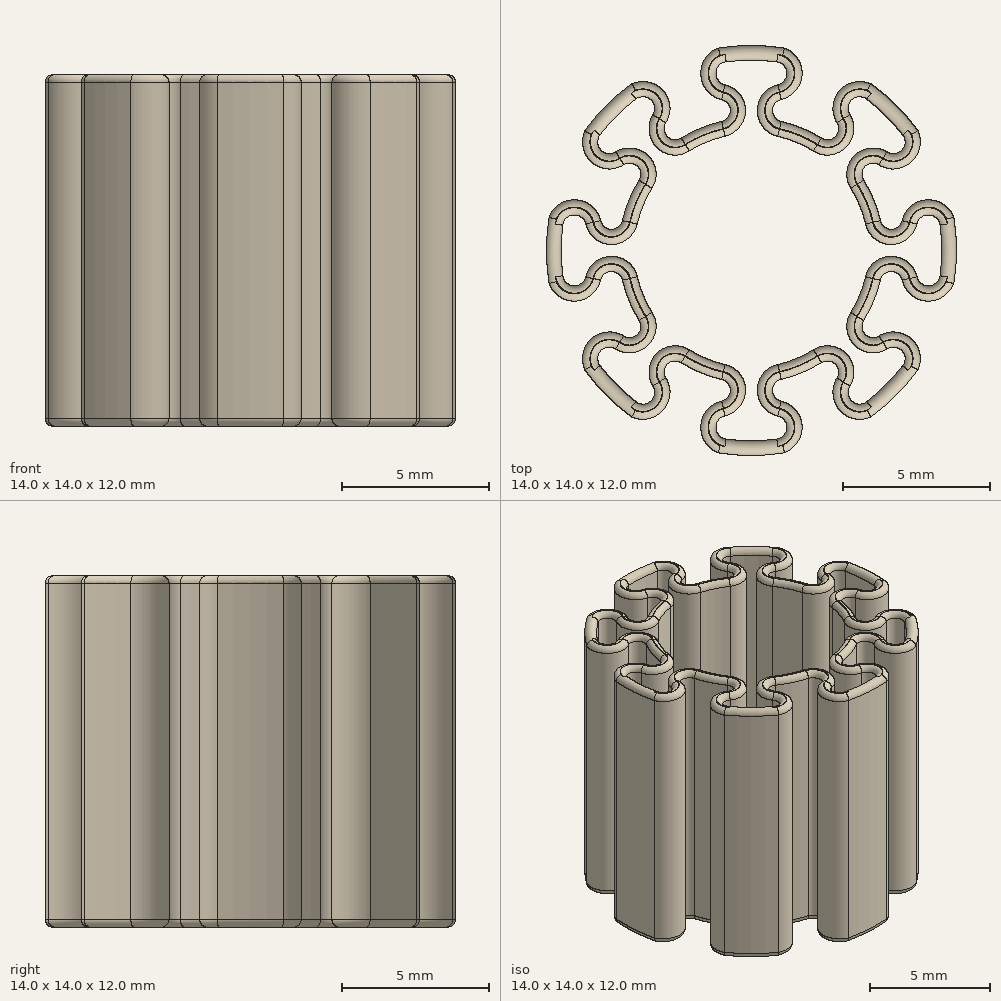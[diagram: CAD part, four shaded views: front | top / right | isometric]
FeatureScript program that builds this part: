
annotation { "Feature Type Name" : "Feature", "Feature Type Description" : "" }
export const myFeature = defineFeature(function(context is Context, id is Id, definition is map)
    precondition{}
    {
        {
            var Q0;
            Q0=qCreatedBy(makeId("Top.planeOp"),FACE);
            var sketch = newSketch(context, id + "F0", { "sketchPlane" : qUnion([Q0])});
            skArc(sketch, "E0", {"start": v(-4.08, 5.68) * mm, "mid": v(-4.95, 4.95) * mm, "end": v(-5.68, 4.08) * mm});
            skArc(sketch, "E1", {"start": v(-0.9, 3.9) * mm, "mid": v(-1.53, 3.7) * mm, "end": v(-2.12, 3.4) * mm});
            skArc(sketch, "E2", {"start": v(-4.1, 5.36) * mm, "mid": v(-4.77, 4.77) * mm, "end": v(-5.36, 4.1) * mm, "construction": true});
            skArc(sketch, "E3", {"start": v(-0.96, 4.14) * mm, "mid": v(-1.63, 3.93) * mm, "end": v(-2.25, 3.6) * mm, "construction": true});
            skArc(sketch, "E4", {"start": v(0.96, 5.41) * mm, "mid": v(1.46, 6.08) * mm, "end": v(0.9, 6.7) * mm, "construction": true});
            skArc(sketch, "E5", {"start": v(0.96, 5.41) * mm, "mid": v(0.45, 4.78) * mm, "end": v(0.96, 4.14) * mm, "construction": true});
            skArc(sketch, "E6", {"start": v(-0.9, 6.7) * mm, "mid": v(-1.46, 6.08) * mm, "end": v(-0.96, 5.41) * mm, "construction": true});
            skArc(sketch, "E7", {"start": v(-0.96, 4.14) * mm, "mid": v(-0.45, 4.78) * mm, "end": v(-0.96, 5.41) * mm, "construction": true});
            skLineSegment(sketch, "E8", {"start": v(0, 0) * mm, "end": v(0, 7.77) * mm, "construction": true});
            skArc(sketch, "E9.1.0", {"start": v(-3.15, 4.5) * mm, "mid": v(-3.06, 3.7) * mm, "end": v(-2.25, 3.6) * mm, "construction": true});
            skArc(sketch, "E9.1.1", {"start": v(-3.15, 4.5) * mm, "mid": v(-3.26, 5.33) * mm, "end": v(-4.1, 5.36) * mm, "construction": true});
            skArc(sketch, "E9.1.2", {"start": v(-3.6, 2.25) * mm, "mid": v(-3.7, 3.06) * mm, "end": v(-4.5, 3.15) * mm, "construction": true});
            skArc(sketch, "E9.1.3", {"start": v(-5.36, 4.1) * mm, "mid": v(-5.33, 3.26) * mm, "end": v(-4.5, 3.15) * mm, "construction": true});
            skArc(sketch, "E9.2.0", {"start": v(-5.41, 0.96) * mm, "mid": v(-4.78, 0.45) * mm, "end": v(-4.14, 0.96) * mm, "construction": true});
            skArc(sketch, "E9.2.1", {"start": v(-5.41, 0.96) * mm, "mid": v(-6.08, 1.46) * mm, "end": v(-6.7, 0.9) * mm, "construction": true});
            skArc(sketch, "E9.2.2", {"start": v(-4.14, -0.96) * mm, "mid": v(-4.78, -0.45) * mm, "end": v(-5.41, -0.96) * mm, "construction": true});
            skArc(sketch, "E9.2.3", {"start": v(-6.7, -0.9) * mm, "mid": v(-6.08, -1.46) * mm, "end": v(-5.41, -0.96) * mm, "construction": true});
            skArc(sketch, "E9.3.0", {"start": v(-4.5, -3.15) * mm, "mid": v(-3.7, -3.06) * mm, "end": v(-3.6, -2.25) * mm, "construction": true});
            skArc(sketch, "E9.3.1", {"start": v(-4.5, -3.15) * mm, "mid": v(-5.33, -3.26) * mm, "end": v(-5.36, -4.1) * mm, "construction": true});
            skArc(sketch, "E9.3.2", {"start": v(-2.25, -3.6) * mm, "mid": v(-3.06, -3.7) * mm, "end": v(-3.15, -4.5) * mm, "construction": true});
            skArc(sketch, "E9.3.3", {"start": v(-4.1, -5.36) * mm, "mid": v(-3.26, -5.33) * mm, "end": v(-3.15, -4.5) * mm, "construction": true});
            skArc(sketch, "E9.4.0", {"start": v(-0.96, -5.41) * mm, "mid": v(-0.45, -4.78) * mm, "end": v(-0.96, -4.14) * mm, "construction": true});
            skArc(sketch, "E9.4.1", {"start": v(-0.96, -5.41) * mm, "mid": v(-1.46, -6.08) * mm, "end": v(-0.9, -6.7) * mm, "construction": true});
            skArc(sketch, "E9.4.2", {"start": v(0.96, -4.14) * mm, "mid": v(0.45, -4.78) * mm, "end": v(0.96, -5.41) * mm, "construction": true});
            skArc(sketch, "E9.4.3", {"start": v(0.9, -6.7) * mm, "mid": v(1.46, -6.08) * mm, "end": v(0.96, -5.41) * mm, "construction": true});
            skArc(sketch, "E9.5.0", {"start": v(3.15, -4.5) * mm, "mid": v(3.06, -3.7) * mm, "end": v(2.25, -3.6) * mm, "construction": true});
            skArc(sketch, "E9.5.1", {"start": v(3.15, -4.5) * mm, "mid": v(3.26, -5.33) * mm, "end": v(4.1, -5.36) * mm, "construction": true});
            skArc(sketch, "E9.5.2", {"start": v(3.6, -2.25) * mm, "mid": v(3.7, -3.06) * mm, "end": v(4.5, -3.15) * mm, "construction": true});
            skArc(sketch, "E9.5.3", {"start": v(5.36, -4.1) * mm, "mid": v(5.33, -3.26) * mm, "end": v(4.5, -3.15) * mm, "construction": true});
            skArc(sketch, "E9.6.0", {"start": v(5.41, -0.96) * mm, "mid": v(4.78, -0.45) * mm, "end": v(4.14, -0.96) * mm, "construction": true});
            skArc(sketch, "E9.6.1", {"start": v(5.41, -0.96) * mm, "mid": v(6.08, -1.46) * mm, "end": v(6.7, -0.9) * mm, "construction": true});
            skArc(sketch, "E9.6.2", {"start": v(4.14, 0.96) * mm, "mid": v(4.78, 0.45) * mm, "end": v(5.41, 0.96) * mm, "construction": true});
            skArc(sketch, "E9.6.3", {"start": v(6.7, 0.9) * mm, "mid": v(6.08, 1.46) * mm, "end": v(5.41, 0.96) * mm, "construction": true});
            skArc(sketch, "E9.7.0", {"start": v(4.5, 3.15) * mm, "mid": v(3.7, 3.06) * mm, "end": v(3.6, 2.25) * mm, "construction": true});
            skArc(sketch, "E9.7.1", {"start": v(4.5, 3.15) * mm, "mid": v(5.33, 3.26) * mm, "end": v(5.36, 4.1) * mm, "construction": true});
            skArc(sketch, "E9.7.2", {"start": v(2.25, 3.6) * mm, "mid": v(3.06, 3.7) * mm, "end": v(3.15, 4.5) * mm, "construction": true});
            skArc(sketch, "E9.7.3", {"start": v(4.1, 5.36) * mm, "mid": v(3.26, 5.33) * mm, "end": v(3.15, 4.5) * mm, "construction": true});
            skLineSegment(sketch, "E10", {"start": v(-0.8, 6.04) * mm, "end": v(0.8, 6.04) * mm, "construction": true});
            skLineSegment(sketch, "E11", {"start": v(1.1, 4.78) * mm, "end": v(2.6, 4.16) * mm, "construction": true});
            skArc(sketch, "E12.trimOffspring", {"start": v(2.25, 3.6) * mm, "mid": v(1.63, 3.93) * mm, "end": v(0.96, 4.14) * mm, "construction": true});
            skArc(sketch, "E13.trimOffspring", {"start": v(4.14, 0.96) * mm, "mid": v(3.93, 1.63) * mm, "end": v(3.6, 2.25) * mm, "construction": true});
            skArc(sketch, "E14.trimOffspring", {"start": v(3.6, -2.25) * mm, "mid": v(3.93, -1.63) * mm, "end": v(4.14, -0.96) * mm, "construction": true});
            skArc(sketch, "E15.trimOffspring", {"start": v(0.96, -4.14) * mm, "mid": v(1.63, -3.93) * mm, "end": v(2.25, -3.6) * mm, "construction": true});
            skArc(sketch, "E16.trimOffspring", {"start": v(-2.25, -3.6) * mm, "mid": v(-1.63, -3.93) * mm, "end": v(-0.96, -4.14) * mm, "construction": true});
            skArc(sketch, "E17.trimOffspring", {"start": v(-4.14, -0.96) * mm, "mid": v(-3.93, -1.63) * mm, "end": v(-3.6, -2.25) * mm, "construction": true});
            skArc(sketch, "E18.trimOffspring", {"start": v(-3.6, 2.25) * mm, "mid": v(-3.93, 1.63) * mm, "end": v(-4.14, 0.96) * mm, "construction": true});
            skArc(sketch, "E19.trimOffspring", {"start": v(0.9, 6.7) * mm, "mid": v(0, 6.75) * mm, "end": v(-0.9, 6.7) * mm, "construction": true});
            skArc(sketch, "E20.trimOffspring", {"start": v(5.36, 4.1) * mm, "mid": v(4.77, 4.77) * mm, "end": v(4.1, 5.36) * mm, "construction": true});
            skArc(sketch, "E21.trimOffspring", {"start": v(6.7, -0.9) * mm, "mid": v(6.75, 0) * mm, "end": v(6.7, 0.9) * mm, "construction": true});
            skArc(sketch, "E22.trimOffspring", {"start": v(4.1, -5.36) * mm, "mid": v(4.77, -4.77) * mm, "end": v(5.36, -4.1) * mm, "construction": true});
            skArc(sketch, "E23.trimOffspring", {"start": v(-0.9, -6.7) * mm, "mid": v(0, -6.75) * mm, "end": v(0.9, -6.7) * mm, "construction": true});
            skArc(sketch, "E24.trimOffspring", {"start": v(-5.36, -4.1) * mm, "mid": v(-4.77, -4.77) * mm, "end": v(-4.1, -5.36) * mm, "construction": true});
            skArc(sketch, "E25.trimOffspring", {"start": v(-6.7, 0.9) * mm, "mid": v(-6.75, 0) * mm, "end": v(-6.7, -0.9) * mm, "construction": true});
            skArc(sketch, "E26.0", {"start": v(-2.92, 4.36) * mm, "mid": v(-3.08, 5.53) * mm, "end": v(-4.26, 5.58) * mm});
            skArc(sketch, "E26.1", {"start": v(-2.92, 4.36) * mm, "mid": v(-2.87, 3.89) * mm, "end": v(-2.4, 3.83) * mm});
            skArc(sketch, "E26.2", {"start": v(1.02, -4.4) * mm, "mid": v(1.73, -4.18) * mm, "end": v(2.4, -3.83) * mm});
            skArc(sketch, "E26.3", {"start": v(1.02, -4.4) * mm, "mid": v(0.72, -4.78) * mm, "end": v(1.02, -5.15) * mm});
            skArc(sketch, "E26.4", {"start": v(0.93, -6.96) * mm, "mid": v(1.73, -6.09) * mm, "end": v(1.02, -5.15) * mm});
            skArc(sketch, "E26.5", {"start": v(-0.93, -6.96) * mm, "mid": v(0, -7.02) * mm, "end": v(0.93, -6.96) * mm});
            skArc(sketch, "E26.6", {"start": v(-1.02, -5.15) * mm, "mid": v(-1.73, -6.09) * mm, "end": v(-0.93, -6.96) * mm});
            skArc(sketch, "E26.7", {"start": v(-1.02, -5.15) * mm, "mid": v(-0.72, -4.78) * mm, "end": v(-1.02, -4.4) * mm});
            skArc(sketch, "E26.8", {"start": v(-2.4, -3.83) * mm, "mid": v(-1.73, -4.18) * mm, "end": v(-1.02, -4.4) * mm});
            skArc(sketch, "E26.9", {"start": v(-2.4, -3.83) * mm, "mid": v(-2.87, -3.89) * mm, "end": v(-2.92, -4.36) * mm});
            skArc(sketch, "E26.10", {"start": v(-4.26, -5.58) * mm, "mid": v(-3.08, -5.53) * mm, "end": v(-2.92, -4.36) * mm});
            skArc(sketch, "E26.11", {"start": v(-5.58, -4.26) * mm, "mid": v(-4.96, -4.96) * mm, "end": v(-4.26, -5.58) * mm});
            skArc(sketch, "E26.12", {"start": v(-4.36, -2.92) * mm, "mid": v(-5.53, -3.08) * mm, "end": v(-5.58, -4.26) * mm});
            skArc(sketch, "E26.13", {"start": v(-4.36, -2.92) * mm, "mid": v(-3.89, -2.87) * mm, "end": v(-3.83, -2.4) * mm});
            skArc(sketch, "E26.14", {"start": v(-3.83, 2.4) * mm, "mid": v(-4.18, 1.73) * mm, "end": v(-4.4, 1.02) * mm});
            skArc(sketch, "E26.15", {"start": v(-3.83, 2.4) * mm, "mid": v(-3.89, 2.87) * mm, "end": v(-4.36, 2.92) * mm});
            skArc(sketch, "E26.16", {"start": v(-5.58, 4.26) * mm, "mid": v(-5.53, 3.08) * mm, "end": v(-4.36, 2.92) * mm});
            skArc(sketch, "E26.17", {"start": v(-4.26, 5.58) * mm, "mid": v(-4.96, 4.96) * mm, "end": v(-5.58, 4.26) * mm});
            skArc(sketch, "E26.18", {"start": v(-5.15, 1.02) * mm, "mid": v(-4.78, 0.72) * mm, "end": v(-4.4, 1.02) * mm});
            skArc(sketch, "E26.19", {"start": v(-5.15, 1.02) * mm, "mid": v(-6.09, 1.73) * mm, "end": v(-6.96, 0.93) * mm});
            skArc(sketch, "E26.20", {"start": v(-6.96, 0.93) * mm, "mid": v(-7.02, 0) * mm, "end": v(-6.96, -0.93) * mm});
            skArc(sketch, "E26.21", {"start": v(-6.96, -0.93) * mm, "mid": v(-6.09, -1.73) * mm, "end": v(-5.15, -1.02) * mm});
            skArc(sketch, "E26.22", {"start": v(-4.4, -1.02) * mm, "mid": v(-4.78, -0.72) * mm, "end": v(-5.15, -1.02) * mm});
            skArc(sketch, "E26.23", {"start": v(-4.4, -1.02) * mm, "mid": v(-4.18, -1.73) * mm, "end": v(-3.83, -2.4) * mm});
            skArc(sketch, "E26.24", {"start": v(2.92, -4.36) * mm, "mid": v(2.87, -3.89) * mm, "end": v(2.4, -3.83) * mm});
            skArc(sketch, "E26.25", {"start": v(2.92, -4.36) * mm, "mid": v(3.08, -5.53) * mm, "end": v(4.26, -5.58) * mm});
            skArc(sketch, "E26.26", {"start": v(4.26, -5.58) * mm, "mid": v(4.96, -4.96) * mm, "end": v(5.58, -4.26) * mm});
            skArc(sketch, "E26.27", {"start": v(5.58, -4.26) * mm, "mid": v(5.53, -3.08) * mm, "end": v(4.36, -2.92) * mm});
            skArc(sketch, "E26.28", {"start": v(3.83, -2.4) * mm, "mid": v(3.89, -2.87) * mm, "end": v(4.36, -2.92) * mm});
            skArc(sketch, "E26.29", {"start": v(3.83, -2.4) * mm, "mid": v(4.18, -1.73) * mm, "end": v(4.4, -1.02) * mm});
            skArc(sketch, "E26.30", {"start": v(5.15, -1.02) * mm, "mid": v(4.78, -0.72) * mm, "end": v(4.4, -1.02) * mm});
            skArc(sketch, "E26.31", {"start": v(5.15, -1.02) * mm, "mid": v(6.09, -1.73) * mm, "end": v(6.96, -0.93) * mm});
            skArc(sketch, "E26.32", {"start": v(6.96, -0.93) * mm, "mid": v(7.02, 0) * mm, "end": v(6.96, 0.93) * mm});
            skArc(sketch, "E26.33", {"start": v(6.96, 0.93) * mm, "mid": v(6.09, 1.73) * mm, "end": v(5.15, 1.02) * mm});
            skArc(sketch, "E26.34", {"start": v(4.4, 1.02) * mm, "mid": v(4.78, 0.72) * mm, "end": v(5.15, 1.02) * mm});
            skArc(sketch, "E26.35", {"start": v(4.4, 1.02) * mm, "mid": v(4.18, 1.73) * mm, "end": v(3.83, 2.4) * mm});
            skArc(sketch, "E26.36", {"start": v(4.36, 2.92) * mm, "mid": v(3.89, 2.87) * mm, "end": v(3.83, 2.4) * mm});
            skArc(sketch, "E26.37", {"start": v(4.36, 2.92) * mm, "mid": v(5.53, 3.08) * mm, "end": v(5.58, 4.26) * mm});
            skArc(sketch, "E26.38", {"start": v(5.58, 4.26) * mm, "mid": v(4.96, 4.96) * mm, "end": v(4.26, 5.58) * mm});
            skArc(sketch, "E26.39", {"start": v(4.26, 5.58) * mm, "mid": v(3.08, 5.53) * mm, "end": v(2.92, 4.36) * mm});
            skArc(sketch, "E26.40", {"start": v(2.4, 3.83) * mm, "mid": v(2.87, 3.89) * mm, "end": v(2.92, 4.36) * mm});
            skArc(sketch, "E26.41", {"start": v(2.4, 3.83) * mm, "mid": v(1.73, 4.18) * mm, "end": v(1.02, 4.4) * mm});
            skArc(sketch, "E26.42", {"start": v(1.02, 5.15) * mm, "mid": v(0.72, 4.78) * mm, "end": v(1.02, 4.4) * mm});
            skArc(sketch, "E26.43", {"start": v(1.02, 5.15) * mm, "mid": v(1.73, 6.09) * mm, "end": v(0.93, 6.96) * mm});
            skArc(sketch, "E26.44", {"start": v(0.93, 6.96) * mm, "mid": v(0, 7.02) * mm, "end": v(-0.93, 6.96) * mm});
            skArc(sketch, "E26.45", {"start": v(-0.93, 6.96) * mm, "mid": v(-1.73, 6.09) * mm, "end": v(-1.02, 5.15) * mm});
            skArc(sketch, "E26.46", {"start": v(-1.02, 4.4) * mm, "mid": v(-0.72, 4.78) * mm, "end": v(-1.02, 5.15) * mm});
            skArc(sketch, "E26.47", {"start": v(-1.02, 4.4) * mm, "mid": v(-1.73, 4.18) * mm, "end": v(-2.4, 3.83) * mm});
            skArc(sketch, "E27.1", {"start": v(-0.9, 3.9) * mm, "mid": v(-0.2, 4.78) * mm, "end": v(-0.9, 5.65) * mm});
            skArc(sketch, "E27.2", {"start": v(0.86, -6.44) * mm, "mid": v(1.21, -6.06) * mm, "end": v(0.9, -5.65) * mm});
            skArc(sketch, "E27.3", {"start": v(-0.86, -6.44) * mm, "mid": v(0, -6.5) * mm, "end": v(0.86, -6.44) * mm});
            skArc(sketch, "E27.4", {"start": v(-0.9, -5.65) * mm, "mid": v(-1.21, -6.06) * mm, "end": v(-0.86, -6.44) * mm});
            skArc(sketch, "E27.5", {"start": v(-0.9, -5.65) * mm, "mid": v(-0.2, -4.78) * mm, "end": v(-0.9, -3.9) * mm});
            skArc(sketch, "E27.6", {"start": v(-2.12, -3.4) * mm, "mid": v(-1.53, -3.7) * mm, "end": v(-0.9, -3.9) * mm});
            skArc(sketch, "E27.7", {"start": v(-2.12, -3.4) * mm, "mid": v(-3.23, -3.52) * mm, "end": v(-3.36, -4.63) * mm});
            skArc(sketch, "E27.8", {"start": v(-3.95, -5.17) * mm, "mid": v(-3.43, -5.14) * mm, "end": v(-3.36, -4.63) * mm});
            skArc(sketch, "E27.9", {"start": v(-5.17, -3.95) * mm, "mid": v(-4.6, -4.6) * mm, "end": v(-3.95, -5.17) * mm});
            skArc(sketch, "E27.10", {"start": v(-4.63, -3.36) * mm, "mid": v(-5.14, -3.43) * mm, "end": v(-5.17, -3.95) * mm});
            skArc(sketch, "E27.11", {"start": v(-4.63, -3.36) * mm, "mid": v(-3.52, -3.23) * mm, "end": v(-3.4, -2.12) * mm});
            skArc(sketch, "E27.12", {"start": v(-3.9, -0.9) * mm, "mid": v(-3.7, -1.53) * mm, "end": v(-3.4, -2.12) * mm});
            skArc(sketch, "E27.13", {"start": v(-3.9, -0.9) * mm, "mid": v(-4.78, -0.2) * mm, "end": v(-5.65, -0.9) * mm});
            skArc(sketch, "E27.14", {"start": v(-5.17, 3.95) * mm, "mid": v(-5.14, 3.43) * mm, "end": v(-4.63, 3.36) * mm});
            skArc(sketch, "E27.15", {"start": v(-3.95, 5.17) * mm, "mid": v(-4.6, 4.6) * mm, "end": v(-5.17, 3.95) * mm});
            skArc(sketch, "E27.16", {"start": v(-3.36, 4.63) * mm, "mid": v(-3.43, 5.14) * mm, "end": v(-3.95, 5.17) * mm});
            skArc(sketch, "E27.17", {"start": v(-3.36, 4.63) * mm, "mid": v(-3.23, 3.52) * mm, "end": v(-2.12, 3.4) * mm});
            skArc(sketch, "E27.18", {"start": v(-3.4, 2.12) * mm, "mid": v(-3.52, 3.23) * mm, "end": v(-4.63, 3.36) * mm});
            skArc(sketch, "E27.19", {"start": v(-3.4, 2.12) * mm, "mid": v(-3.7, 1.53) * mm, "end": v(-3.9, 0.9) * mm});
            skArc(sketch, "E27.20", {"start": v(-5.65, 0.9) * mm, "mid": v(-4.78, 0.2) * mm, "end": v(-3.9, 0.9) * mm});
            skArc(sketch, "E27.21", {"start": v(-5.65, 0.9) * mm, "mid": v(-6.06, 1.21) * mm, "end": v(-6.44, 0.86) * mm});
            skArc(sketch, "E27.22", {"start": v(-6.44, 0.86) * mm, "mid": v(-6.5, 0) * mm, "end": v(-6.44, -0.86) * mm});
            skArc(sketch, "E27.23", {"start": v(-6.44, -0.86) * mm, "mid": v(-6.06, -1.21) * mm, "end": v(-5.65, -0.9) * mm});
            skArc(sketch, "E27.24", {"start": v(0.9, -3.9) * mm, "mid": v(0.2, -4.78) * mm, "end": v(0.9, -5.65) * mm});
            skArc(sketch, "E27.25", {"start": v(0.9, -3.9) * mm, "mid": v(1.53, -3.7) * mm, "end": v(2.12, -3.4) * mm});
            skArc(sketch, "E27.26", {"start": v(3.36, -4.63) * mm, "mid": v(3.23, -3.52) * mm, "end": v(2.12, -3.4) * mm});
            skArc(sketch, "E27.27", {"start": v(3.36, -4.63) * mm, "mid": v(3.43, -5.14) * mm, "end": v(3.95, -5.17) * mm});
            skArc(sketch, "E27.28", {"start": v(3.95, -5.17) * mm, "mid": v(4.6, -4.6) * mm, "end": v(5.17, -3.95) * mm});
            skArc(sketch, "E27.29", {"start": v(5.17, -3.95) * mm, "mid": v(5.14, -3.43) * mm, "end": v(4.63, -3.36) * mm});
            skArc(sketch, "E27.30", {"start": v(3.4, -2.12) * mm, "mid": v(3.52, -3.23) * mm, "end": v(4.63, -3.36) * mm});
            skArc(sketch, "E27.31", {"start": v(3.4, -2.12) * mm, "mid": v(3.7, -1.53) * mm, "end": v(3.9, -0.9) * mm});
            skArc(sketch, "E27.32", {"start": v(5.65, -0.9) * mm, "mid": v(4.78, -0.2) * mm, "end": v(3.9, -0.9) * mm});
            skArc(sketch, "E27.33", {"start": v(5.65, -0.9) * mm, "mid": v(6.06, -1.21) * mm, "end": v(6.44, -0.86) * mm});
            skArc(sketch, "E27.34", {"start": v(6.44, -0.86) * mm, "mid": v(6.5, 0) * mm, "end": v(6.44, 0.86) * mm});
            skArc(sketch, "E27.35", {"start": v(6.44, 0.86) * mm, "mid": v(6.06, 1.21) * mm, "end": v(5.65, 0.9) * mm});
            skArc(sketch, "E27.36", {"start": v(3.9, 0.9) * mm, "mid": v(4.78, 0.2) * mm, "end": v(5.65, 0.9) * mm});
            skArc(sketch, "E27.37", {"start": v(3.9, 0.9) * mm, "mid": v(3.7, 1.53) * mm, "end": v(3.4, 2.12) * mm});
            skArc(sketch, "E27.38", {"start": v(4.63, 3.36) * mm, "mid": v(3.52, 3.23) * mm, "end": v(3.4, 2.12) * mm});
            skArc(sketch, "E27.39", {"start": v(4.63, 3.36) * mm, "mid": v(5.14, 3.43) * mm, "end": v(5.17, 3.95) * mm});
            skArc(sketch, "E27.40", {"start": v(5.17, 3.95) * mm, "mid": v(4.6, 4.6) * mm, "end": v(3.95, 5.17) * mm});
            skArc(sketch, "E27.41", {"start": v(3.95, 5.17) * mm, "mid": v(3.43, 5.14) * mm, "end": v(3.36, 4.63) * mm});
            skArc(sketch, "E27.42", {"start": v(2.12, 3.4) * mm, "mid": v(3.23, 3.52) * mm, "end": v(3.36, 4.63) * mm});
            skArc(sketch, "E27.43", {"start": v(2.12, 3.4) * mm, "mid": v(1.53, 3.7) * mm, "end": v(0.9, 3.9) * mm});
            skArc(sketch, "E27.44", {"start": v(0.9, 5.65) * mm, "mid": v(0.2, 4.78) * mm, "end": v(0.9, 3.9) * mm});
            skArc(sketch, "E27.45", {"start": v(0.9, 5.65) * mm, "mid": v(1.21, 6.06) * mm, "end": v(0.86, 6.44) * mm});
            skArc(sketch, "E27.46", {"start": v(0.86, 6.44) * mm, "mid": v(0, 6.5) * mm, "end": v(-0.86, 6.44) * mm});
            skArc(sketch, "E27.47", {"start": v(-0.86, 6.44) * mm, "mid": v(-1.21, 6.06) * mm, "end": v(-0.9, 5.65) * mm});
            skArc(sketch, "E28.trimOffspring", {"start": v(1.13, 6.9) * mm, "mid": v(0, 7) * mm, "end": v(-1.13, 6.9) * mm});
            skArc(sketch, "E29.trimOffspring", {"start": v(5.68, 4.08) * mm, "mid": v(4.95, 4.95) * mm, "end": v(4.08, 5.68) * mm});
            skArc(sketch, "E30.trimOffspring", {"start": v(6.9, -1.13) * mm, "mid": v(7, 0) * mm, "end": v(6.9, 1.13) * mm});
            skArc(sketch, "E31.trimOffspring", {"start": v(4.08, -5.68) * mm, "mid": v(4.95, -4.95) * mm, "end": v(5.68, -4.08) * mm});
            skArc(sketch, "E32.trimOffspring", {"start": v(-1.13, -6.9) * mm, "mid": v(0, -7) * mm, "end": v(1.13, -6.9) * mm});
            skArc(sketch, "E33.trimOffspring", {"start": v(-5.68, -4.08) * mm, "mid": v(-4.95, -4.95) * mm, "end": v(-4.08, -5.68) * mm});
            skArc(sketch, "E34.trimOffspring", {"start": v(-6.9, 1.13) * mm, "mid": v(-7, 0) * mm, "end": v(-6.9, -1.13) * mm});
            skSolve(sketch);
        }
        {
            var Q0;
            {var subQ27=sQuery(id+"F0.wireOp",EDGE,"E0");Q0=makeQuery(id+"F0.imprint","IMPRINT",FACE,{"disambiguationData":[TD([[makeQuery(id+"F0.imprint","IMPRINT",EDGE,{"derivedFrom":subQ27}),1.0]])]});}
            extrude(context, id + "F1", {"entities" : qUnion([Q0]), "depth" : 12 * mm, "offsetDistance" : 25 * mm});
        }
        {
            var Q0;
            Q0=makeQuery(id+"F1.opExtrude","CAP_FACE",FACE,{"disambiguationData":[OSD([sQuery(id+"F0.wireOp",EDGE,"E0"),sQuery(id+"F0.wireOp",EDGE,"E26.0"),sQuery(id+"F0.wireOp",EDGE,"E26.1"),sQuery(id+"F0.wireOp",EDGE,"E26.2"),sQuery(id+"F0.wireOp",EDGE,"E26.3"),sQuery(id+"F0.wireOp",EDGE,"E26.4"),sQuery(id+"F0.wireOp",EDGE,"E26.6"),sQuery(id+"F0.wireOp",EDGE,"E26.7"),sQuery(id+"F0.wireOp",EDGE,"E26.8"),sQuery(id+"F0.wireOp",EDGE,"E26.9"),sQuery(id+"F0.wireOp",EDGE,"E26.10"),sQuery(id+"F0.wireOp",EDGE,"E26.12"),sQuery(id+"F0.wireOp",EDGE,"E26.13"),sQuery(id+"F0.wireOp",EDGE,"E26.14"),sQuery(id+"F0.wireOp",EDGE,"E26.15"),sQuery(id+"F0.wireOp",EDGE,"E26.16"),sQuery(id+"F0.wireOp",EDGE,"E26.18"),sQuery(id+"F0.wireOp",EDGE,"E26.19"),sQuery(id+"F0.wireOp",EDGE,"E26.21"),sQuery(id+"F0.wireOp",EDGE,"E26.22"),sQuery(id+"F0.wireOp",EDGE,"E26.23"),sQuery(id+"F0.wireOp",EDGE,"E26.24"),sQuery(id+"F0.wireOp",EDGE,"E26.25"),sQuery(id+"F0.wireOp",EDGE,"E26.27"),sQuery(id+"F0.wireOp",EDGE,"E26.28"),sQuery(id+"F0.wireOp",EDGE,"E26.29"),sQuery(id+"F0.wireOp",EDGE,"E26.30"),sQuery(id+"F0.wireOp",EDGE,"E26.31"),sQuery(id+"F0.wireOp",EDGE,"E26.33"),sQuery(id+"F0.wireOp",EDGE,"E26.34"),sQuery(id+"F0.wireOp",EDGE,"E26.35"),sQuery(id+"F0.wireOp",EDGE,"E26.36"),sQuery(id+"F0.wireOp",EDGE,"E26.37"),sQuery(id+"F0.wireOp",EDGE,"E26.39"),sQuery(id+"F0.wireOp",EDGE,"E26.40"),sQuery(id+"F0.wireOp",EDGE,"E26.41"),sQuery(id+"F0.wireOp",EDGE,"E26.42"),sQuery(id+"F0.wireOp",EDGE,"E26.43"),sQuery(id+"F0.wireOp",EDGE,"E26.45"),sQuery(id+"F0.wireOp",EDGE,"E26.46"),sQuery(id+"F0.wireOp",EDGE,"E26.47"),sQuery(id+"F0.wireOp",EDGE,"E1"),sQuery(id+"F0.wireOp",EDGE,"E27.1"),sQuery(id+"F0.wireOp",EDGE,"E27.2"),sQuery(id+"F0.wireOp",EDGE,"E27.3"),sQuery(id+"F0.wireOp",EDGE,"E27.4"),sQuery(id+"F0.wireOp",EDGE,"E27.5"),sQuery(id+"F0.wireOp",EDGE,"E27.7"),sQuery(id+"F0.wireOp",EDGE,"E27.8"),sQuery(id+"F0.wireOp",EDGE,"E27.9"),sQuery(id+"F0.wireOp",EDGE,"E27.10"),sQuery(id+"F0.wireOp",EDGE,"E27.11"),sQuery(id+"F0.wireOp",EDGE,"E27.13"),sQuery(id+"F0.wireOp",EDGE,"E27.14"),sQuery(id+"F0.wireOp",EDGE,"E27.15"),sQuery(id+"F0.wireOp",EDGE,"E27.16"),sQuery(id+"F0.wireOp",EDGE,"E27.17"),sQuery(id+"F0.wireOp",EDGE,"E27.18"),sQuery(id+"F0.wireOp",EDGE,"E27.19"),sQuery(id+"F0.wireOp",EDGE,"E27.20"),sQuery(id+"F0.wireOp",EDGE,"E27.21"),sQuery(id+"F0.wireOp",EDGE,"E27.22"),sQuery(id+"F0.wireOp",EDGE,"E27.23"),sQuery(id+"F0.wireOp",EDGE,"E27.24"),sQuery(id+"F0.wireOp",EDGE,"E27.26"),sQuery(id+"F0.wireOp",EDGE,"E27.27"),sQuery(id+"F0.wireOp",EDGE,"E27.28"),sQuery(id+"F0.wireOp",EDGE,"E27.29"),sQuery(id+"F0.wireOp",EDGE,"E27.30"),sQuery(id+"F0.wireOp",EDGE,"E27.32"),sQuery(id+"F0.wireOp",EDGE,"E27.33"),sQuery(id+"F0.wireOp",EDGE,"E27.34"),sQuery(id+"F0.wireOp",EDGE,"E27.35"),sQuery(id+"F0.wireOp",EDGE,"E27.36"),sQuery(id+"F0.wireOp",EDGE,"E27.38"),sQuery(id+"F0.wireOp",EDGE,"E27.39"),sQuery(id+"F0.wireOp",EDGE,"E27.40"),sQuery(id+"F0.wireOp",EDGE,"E27.41"),sQuery(id+"F0.wireOp",EDGE,"E27.42"),sQuery(id+"F0.wireOp",EDGE,"E27.44"),sQuery(id+"F0.wireOp",EDGE,"E27.45"),sQuery(id+"F0.wireOp",EDGE,"E27.46"),sQuery(id+"F0.wireOp",EDGE,"E27.47"),sQuery(id+"F0.wireOp",EDGE,"E28.trimOffspring"),sQuery(id+"F0.wireOp",EDGE,"E29.trimOffspring"),sQuery(id+"F0.wireOp",EDGE,"E30.trimOffspring"),sQuery(id+"F0.wireOp",EDGE,"E31.trimOffspring"),sQuery(id+"F0.wireOp",EDGE,"E32.trimOffspring"),sQuery(id+"F0.wireOp",EDGE,"E33.trimOffspring"),sQuery(id+"F0.wireOp",EDGE,"E34.trimOffspring"),sQuery(id+"F0.wireOp",EDGE,"E27.12"),sQuery(id+"F0.wireOp",EDGE,"E27.6"),sQuery(id+"F0.wireOp",EDGE,"E27.25"),sQuery(id+"F0.wireOp",EDGE,"E27.31"),sQuery(id+"F0.wireOp",EDGE,"E27.37"),sQuery(id+"F0.wireOp",EDGE,"E27.43")])],"isStart":false});
            var Q1;
            Q1=makeQuery(id+"F1.opExtrude","CAP_FACE",FACE,{"disambiguationData":[OSD([sQuery(id+"F0.wireOp",EDGE,"E0"),sQuery(id+"F0.wireOp",EDGE,"E26.0"),sQuery(id+"F0.wireOp",EDGE,"E26.1"),sQuery(id+"F0.wireOp",EDGE,"E26.2"),sQuery(id+"F0.wireOp",EDGE,"E26.3"),sQuery(id+"F0.wireOp",EDGE,"E26.4"),sQuery(id+"F0.wireOp",EDGE,"E26.6"),sQuery(id+"F0.wireOp",EDGE,"E26.7"),sQuery(id+"F0.wireOp",EDGE,"E26.8"),sQuery(id+"F0.wireOp",EDGE,"E26.9"),sQuery(id+"F0.wireOp",EDGE,"E26.10"),sQuery(id+"F0.wireOp",EDGE,"E26.12"),sQuery(id+"F0.wireOp",EDGE,"E26.13"),sQuery(id+"F0.wireOp",EDGE,"E26.14"),sQuery(id+"F0.wireOp",EDGE,"E26.15"),sQuery(id+"F0.wireOp",EDGE,"E26.16"),sQuery(id+"F0.wireOp",EDGE,"E26.18"),sQuery(id+"F0.wireOp",EDGE,"E26.19"),sQuery(id+"F0.wireOp",EDGE,"E26.21"),sQuery(id+"F0.wireOp",EDGE,"E26.22"),sQuery(id+"F0.wireOp",EDGE,"E26.23"),sQuery(id+"F0.wireOp",EDGE,"E26.24"),sQuery(id+"F0.wireOp",EDGE,"E26.25"),sQuery(id+"F0.wireOp",EDGE,"E26.27"),sQuery(id+"F0.wireOp",EDGE,"E26.28"),sQuery(id+"F0.wireOp",EDGE,"E26.29"),sQuery(id+"F0.wireOp",EDGE,"E26.30"),sQuery(id+"F0.wireOp",EDGE,"E26.31"),sQuery(id+"F0.wireOp",EDGE,"E26.33"),sQuery(id+"F0.wireOp",EDGE,"E26.34"),sQuery(id+"F0.wireOp",EDGE,"E26.35"),sQuery(id+"F0.wireOp",EDGE,"E26.36"),sQuery(id+"F0.wireOp",EDGE,"E26.37"),sQuery(id+"F0.wireOp",EDGE,"E26.39"),sQuery(id+"F0.wireOp",EDGE,"E26.40"),sQuery(id+"F0.wireOp",EDGE,"E26.41"),sQuery(id+"F0.wireOp",EDGE,"E26.42"),sQuery(id+"F0.wireOp",EDGE,"E26.43"),sQuery(id+"F0.wireOp",EDGE,"E26.45"),sQuery(id+"F0.wireOp",EDGE,"E26.46"),sQuery(id+"F0.wireOp",EDGE,"E26.47"),sQuery(id+"F0.wireOp",EDGE,"E1"),sQuery(id+"F0.wireOp",EDGE,"E27.1"),sQuery(id+"F0.wireOp",EDGE,"E27.2"),sQuery(id+"F0.wireOp",EDGE,"E27.3"),sQuery(id+"F0.wireOp",EDGE,"E27.4"),sQuery(id+"F0.wireOp",EDGE,"E27.5"),sQuery(id+"F0.wireOp",EDGE,"E27.7"),sQuery(id+"F0.wireOp",EDGE,"E27.8"),sQuery(id+"F0.wireOp",EDGE,"E27.9"),sQuery(id+"F0.wireOp",EDGE,"E27.10"),sQuery(id+"F0.wireOp",EDGE,"E27.11"),sQuery(id+"F0.wireOp",EDGE,"E27.13"),sQuery(id+"F0.wireOp",EDGE,"E27.14"),sQuery(id+"F0.wireOp",EDGE,"E27.15"),sQuery(id+"F0.wireOp",EDGE,"E27.16"),sQuery(id+"F0.wireOp",EDGE,"E27.17"),sQuery(id+"F0.wireOp",EDGE,"E27.18"),sQuery(id+"F0.wireOp",EDGE,"E27.19"),sQuery(id+"F0.wireOp",EDGE,"E27.20"),sQuery(id+"F0.wireOp",EDGE,"E27.21"),sQuery(id+"F0.wireOp",EDGE,"E27.22"),sQuery(id+"F0.wireOp",EDGE,"E27.23"),sQuery(id+"F0.wireOp",EDGE,"E27.24"),sQuery(id+"F0.wireOp",EDGE,"E27.26"),sQuery(id+"F0.wireOp",EDGE,"E27.27"),sQuery(id+"F0.wireOp",EDGE,"E27.28"),sQuery(id+"F0.wireOp",EDGE,"E27.29"),sQuery(id+"F0.wireOp",EDGE,"E27.30"),sQuery(id+"F0.wireOp",EDGE,"E27.32"),sQuery(id+"F0.wireOp",EDGE,"E27.33"),sQuery(id+"F0.wireOp",EDGE,"E27.34"),sQuery(id+"F0.wireOp",EDGE,"E27.35"),sQuery(id+"F0.wireOp",EDGE,"E27.36"),sQuery(id+"F0.wireOp",EDGE,"E27.38"),sQuery(id+"F0.wireOp",EDGE,"E27.39"),sQuery(id+"F0.wireOp",EDGE,"E27.40"),sQuery(id+"F0.wireOp",EDGE,"E27.41"),sQuery(id+"F0.wireOp",EDGE,"E27.42"),sQuery(id+"F0.wireOp",EDGE,"E27.44"),sQuery(id+"F0.wireOp",EDGE,"E27.45"),sQuery(id+"F0.wireOp",EDGE,"E27.46"),sQuery(id+"F0.wireOp",EDGE,"E27.47"),sQuery(id+"F0.wireOp",EDGE,"E28.trimOffspring"),sQuery(id+"F0.wireOp",EDGE,"E29.trimOffspring"),sQuery(id+"F0.wireOp",EDGE,"E30.trimOffspring"),sQuery(id+"F0.wireOp",EDGE,"E31.trimOffspring"),sQuery(id+"F0.wireOp",EDGE,"E32.trimOffspring"),sQuery(id+"F0.wireOp",EDGE,"E33.trimOffspring"),sQuery(id+"F0.wireOp",EDGE,"E34.trimOffspring"),sQuery(id+"F0.wireOp",EDGE,"E27.12"),sQuery(id+"F0.wireOp",EDGE,"E27.6"),sQuery(id+"F0.wireOp",EDGE,"E27.25"),sQuery(id+"F0.wireOp",EDGE,"E27.31"),sQuery(id+"F0.wireOp",EDGE,"E27.37"),sQuery(id+"F0.wireOp",EDGE,"E27.43")])],"isStart":true});
            fillet(context, id + "F2", {"entities" : qUnion([Q0, Q1]), "radius" : .25 * mm, "tangentPropagation" : true, "allowEdgeOverflow" : false});
        }
    });
